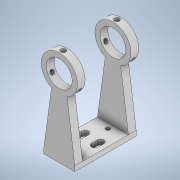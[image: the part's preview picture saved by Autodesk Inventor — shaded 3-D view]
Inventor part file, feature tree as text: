
AUTODESK INVENTOR PART (.ipt)
format: ipt  version: 2021 (Build 250183000, 183)  size: 289,792 bytes
history: native  units: in
note: dims shown in document units (in); Inventor stores cm internally (conversion verified against a paired STEP export)
features: sketch x6, extrude x4, plane x2, hole x2, mirror x2, pattern_circular x1
ambient origin geometry x8: Origin, YZ Plane, XZ Plane, XY Plane, X Axis, Y Axis, Z Axis, Center Point
bodies: Solid1 (feature_tree)
feature tree (17):
  extrude  "Extrusion1"  Depth=0.75in
  extrude  "Extrusion2"  Depth=2.979in TaperAngle=0.0deg
  plane  "Work Plane1"
  extrude  "Extrusion4"  Depth=0.325in
  plane  "Work Plane2"
  hole  "Hole2"  [1 undecoded]
  pattern_circular  "Circular Pattern2"  [2 undecoded]
  extrude  "Extrusion7"  Depth=4.0in
  hole  "Hole1"  [1 undecoded]
  mirror  "Mirror2"
  mirror  "Mirror3"
  sketch  "Sketch1"  dims[d0=6.0in d1=0.75in]
  sketch  "Sketch2"  dims[d2=0.5in d3=2.979in d4=0.0in]
  sketch  "Sketch5"  dims[d5=0.375in d6=0.325in]
  sketch  "Sketch6"  dims[d7=0.6in d8=0.75in]
  sketch  "Sketch20"  dims[d9=0.0in d10=0.0in]
  sketch  "Sketch22"  dims[d15=1.25in d16=0.25in d17=4.0in d18=0.375in d19=0.375in d20=0.0in d51=0.0039in d53=60.0deg d72=0.0039in d74=60.0deg d93=0.0039in d95=60.0deg d114=0.0039in d116=60.0deg d135=0.0039in d137=60.0deg d156=0.0039in d158=60.0deg d168=0.125in d169=0.0in d170=0.325in d173=0.25in d174=0.25in d175=0.201in d176=0.38in d177=0.375in d178=0.125in d179=0.5635in d180=1.0in d181=0.8108in d183=0.625in d185=0.218in d186=0.75in d187=0.249in d188=0.194in d189=0.5635in d190=1.0in d191=0.0in d192=1.1811in d193=360.0deg]
note: 4 required parameter values undecoded (feature->parameter linkage not recoverable at this tier; creation-order binding heuristic only, values carry confidence <= 0.55)
